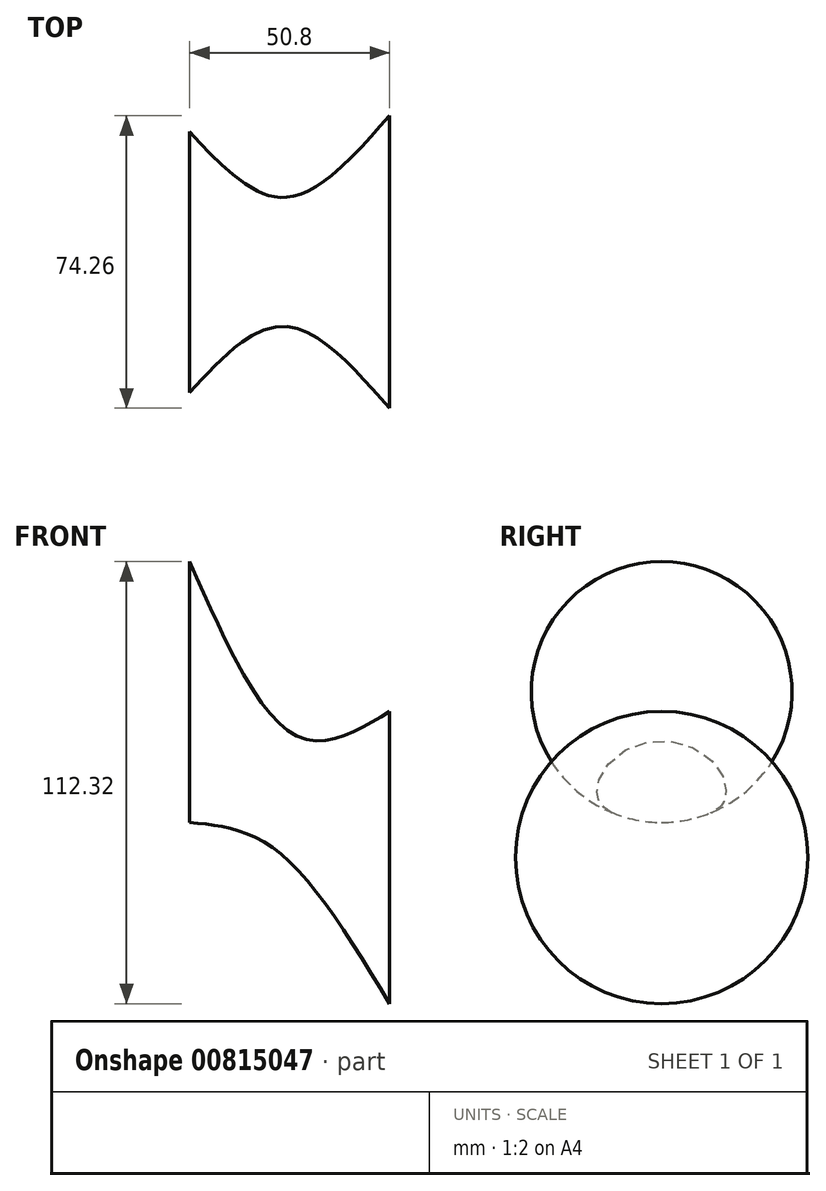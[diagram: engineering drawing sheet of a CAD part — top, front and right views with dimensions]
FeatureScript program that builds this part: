
annotation { "Feature Type Name" : "Feature", "Feature Type Description" : "" }
export const myFeature = defineFeature(function(context is Context, id is Id, definition is map)
    precondition{}
    {
        {
            var Q0;
            Q0=qCreatedBy(makeId("Right.planeOp"),FACE);
            cPlane(context, id + "F0", {"entities" : qUnion([Q0]), "cplaneType" : CPlaneType.OFFSET, "offset" : 25.4 * mm, "width" : 152.4 * mm, "height" : 152.4 * mm});
        }
        {
            var Q0;
            Q0=qCreatedBy(makeId("Right.planeOp"),FACE);
            cPlane(context, id + "F1", {"entities" : qUnion([Q0]), "cplaneType" : CPlaneType.OFFSET, "offset" : 25.4 * mm, "oppositeDirection" : true, "width" : 152.4 * mm, "height" : 152.4 * mm});
        }
        {
            var Q0;
            Q0=qCreatedBy(id+"F0.planeOp",FACE);
            var sketch = newSketch(context, id + "F2", { "sketchPlane" : qUnion([Q0])});
            skCircle(sketch, "E0", {"center": v(0, 0) * mm, "radius": 37.13 * mm});
            skSolve(sketch);
        }
        {
            var Q0;
            Q0=qCreatedBy(id+"F1.planeOp",FACE);
            var sketch = newSketch(context, id + "F3", { "sketchPlane" : qUnion([Q0])});
            skCircle(sketch, "E1", {"center": v(0, 42.06) * mm, "radius": 33.13 * mm});
            skSolve(sketch);
        }
        {
            var Q0;
            Q0=qCreatedBy(makeId("Right.planeOp"),FACE);
            var sketch = newSketch(context, id + "F4", { "sketchPlane" : qUnion([Q0])});
            skCircle(sketch, "E2", {"center": v(0, 15.44) * mm, "radius": 16.5 * mm});
            skSolve(sketch);
        }
        {
            var Q0;
            Q0=makeQuery(id+"F2.imprint","IMPRINT",FACE,{"disambiguationData":[TD([[makeQuery(id+"F2.imprint","IMPRINT",EDGE,{"derivedFrom":sQuery(id+"F2.wireOp",EDGE,"E0")}),1.0]])]});
            var Q1;
            Q1=makeQuery(id+"F4.imprint","IMPRINT",FACE,{"disambiguationData":[TD([[makeQuery(id+"F4.imprint","IMPRINT",EDGE,{"derivedFrom":sQuery(id+"F4.wireOp",EDGE,"E2")}),1.0]])]});
            var Q2;
            Q2=makeQuery(id+"F3.imprint","IMPRINT",FACE,{"disambiguationData":[TD([[makeQuery(id+"F3.imprint","IMPRINT",EDGE,{"derivedFrom":sQuery(id+"F3.wireOp",EDGE,"E1")}),1.0]])]});
            loft(context, id + "F5", {"sheetProfilesArray" : [{ "sheetProfileEntities" : qUnion([Q0]) }, { "sheetProfileEntities" : qUnion([Q1]) }, { "sheetProfileEntities" : qUnion([Q2]) }]});
        }
    });
